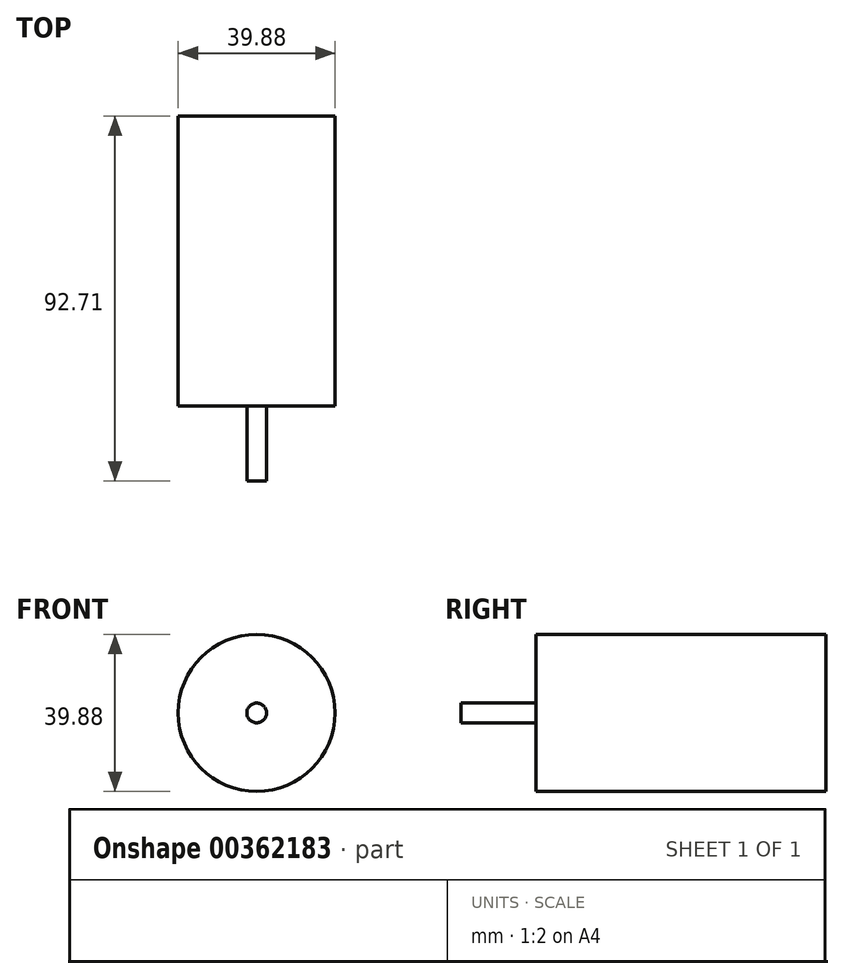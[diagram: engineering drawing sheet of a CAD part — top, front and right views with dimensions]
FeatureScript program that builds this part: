
annotation { "Feature Type Name" : "Feature", "Feature Type Description" : "" }
export const myFeature = defineFeature(function(context is Context, id is Id, definition is map)
    precondition{}
    {
        {
            var Q0;
            Q0=qCreatedBy(makeId("Front.planeOp"),FACE);
            var sketch = newSketch(context, id + "F0", { "sketchPlane" : qUnion([Q0])});
            skCircle(sketch, "E0", {"center": v(0, 0) * mm, "radius": 19.94 * mm});
            skSolve(sketch);
        }
        {
            var Q0;
            Q0=makeQuery(id+"F0.imprint","IMPRINT",FACE,{"disambiguationData":[TD([[makeQuery(id+"F0.imprint","IMPRINT",EDGE,{"derivedFrom":sQuery(id+"F0.wireOp",EDGE,"E0")}),1.0]])]});
            extrude(context, id + "F1", {"entities" : qUnion([Q0]), "depth" : 73.66 * mm, "offsetDistance" : 25.4 * mm});
        }
        {
            var Q0;
            Q0=makeQuery(id+"F1.opExtrude","CAP_FACE",FACE,{"disambiguationData":[OSD([sQuery(id+"F0.wireOp",EDGE,"E0")])],"isStart":false});
            var sketch = newSketch(context, id + "F2", { "sketchPlane" : qUnion([Q0])});
            skCircle(sketch, "E1", {"center": v(0, 0) * mm, "radius": 2.5 * mm});
            skSolve(sketch);
        }
        {
            var Q0;
            Q0=makeQuery(id+"F2.imprint","IMPRINT",FACE,{"disambiguationData":[TD([[makeQuery(id+"F2.imprint","IMPRINT",EDGE,{"derivedFrom":sQuery(id+"F2.wireOp",EDGE,"E1")}),1.0]])]});
            extrude(context, id + "F3", {"entities" : qUnion([Q0]), "operationType" : NewBodyOperationType.ADD, "depth" : 19.05 * mm, "offsetDistance" : 25.4 * mm});
        }
    });
